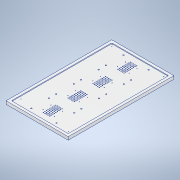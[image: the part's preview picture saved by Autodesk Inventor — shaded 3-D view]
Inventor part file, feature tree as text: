
AUTODESK INVENTOR PART (.ipt)
format: ipt  version: 2022 (Build 260153000, 153)  size: 387,072 bytes
history: native  units: in
note: dims shown in document units (in); Inventor stores cm internally (conversion verified against a paired STEP export)
features: sketch x5, hole x3, extrude x2
ambient origin geometry x8: Origin, YZ Plane, XZ Plane, XY Plane, X Axis, Y Axis, Z Axis, Center Point
bodies: Solid1 (feature_tree)
feature tree (10):
  extrude  "Extrusion1"  Depth=8.5in
  extrude  "Extrusion2"  Depth=0.2106in
  hole  "Hole1"  [1 undecoded]
  hole  "Hole2"  [1 undecoded]
  hole  "Hole3"  [1 undecoded]
  sketch  "Sketch1"  dims[d0=5.0in d1=8.5in]
  sketch  "Sketch2"  dims[d2=0.25in d3=0.0in d4=0.2106in]
  sketch  "Sketch3"  dims[d5=0.2106in d6=0.2106in]
  sketch  "Sketch4"  dims[d7=0.063in d8=0.0in d9=1.2756in]
  sketch  "Sketch5"  dims[d10=0.3287in d11=1.4213in d12=2.0276in d13=1.5748in d15=2.0in d16=0.3937in d18=0.3937in d20=0.0984in d21=0.2362in d22=0.1575in d23=0.0787in d24=90.0deg d25=0.315in d26=0.8108in d27=0.1969in d28=0.5787in d29=0.1969in d30=0.1969in d31=0.1969in d32=0.1969in d33=0.1969in d34=0.1969in d35=1.8262in d36=0.7244in d37=0.6299in d38=0.9264in d39=1.5748in d41=2.0in d42=0.3937in d44=0.3937in d46=0.0402in d47=0.094in d48=0.1575in d49=0.0787in d50=90.0deg d51=0.315in d52=0.8108in d53=0.5394in d54=2.0394in d55=3.5433in d57=0.125in d58=1.9685in d60=0.125in d63=1.5748in d65=2.0in d66=0.3937in d68=0.3937in d70=0.063in d71=0.094in d72=0.1575in d73=0.0787in d74=90.0deg d75=0.315in d76=0.8108in d77=0.0787in d56=0.0295in]
note: 3 required parameter values undecoded (feature->parameter linkage not recoverable at this tier; creation-order binding heuristic only, values carry confidence <= 0.55)
